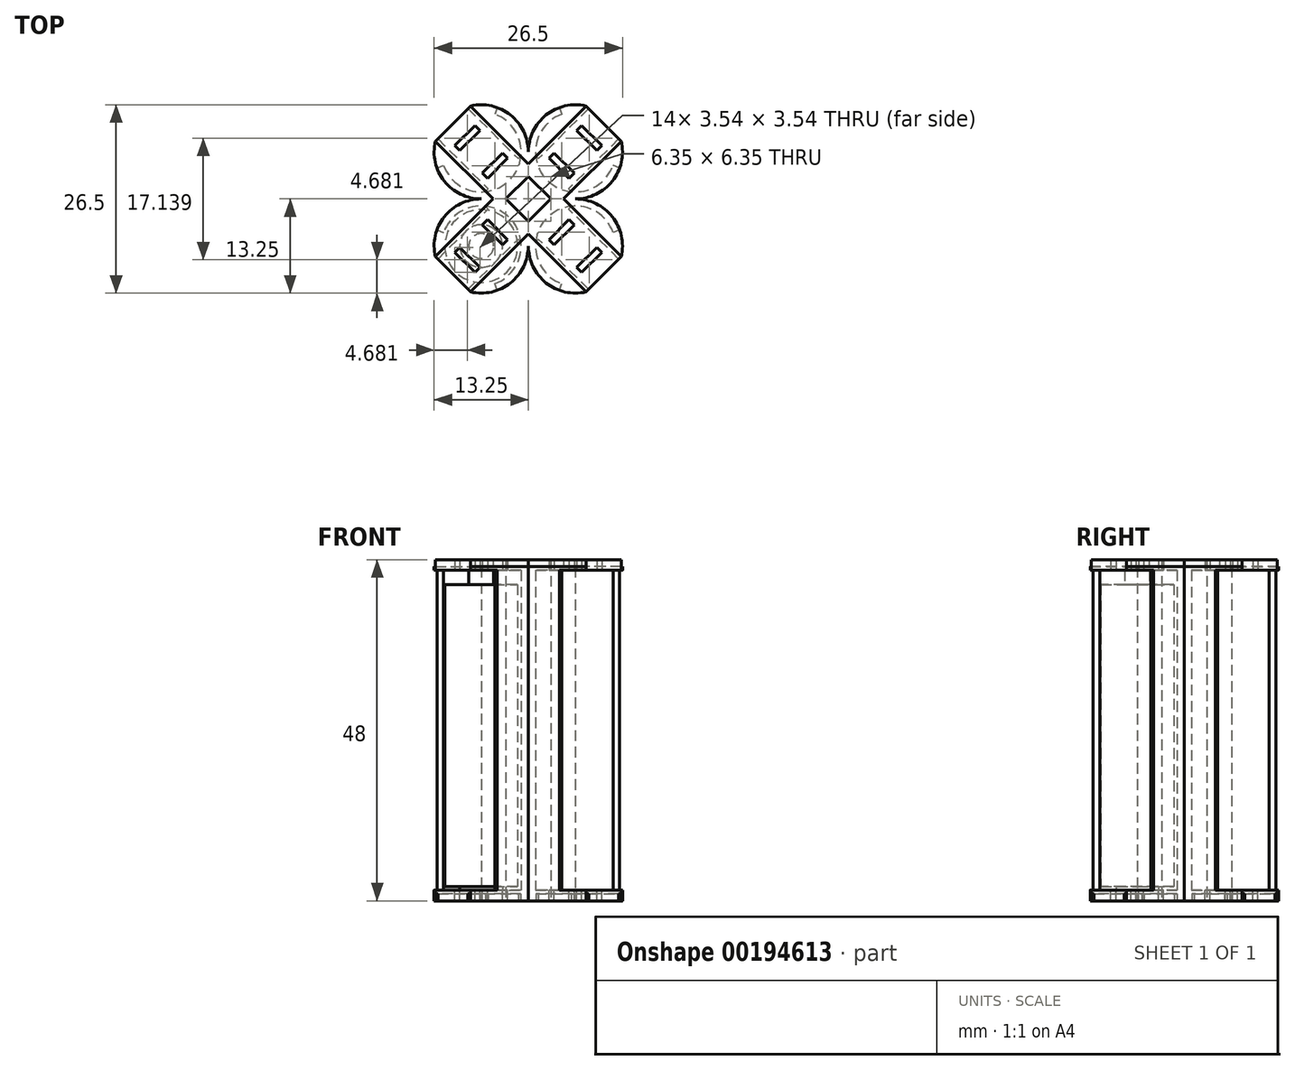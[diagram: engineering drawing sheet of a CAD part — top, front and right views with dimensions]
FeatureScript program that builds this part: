
annotation { "Feature Type Name" : "Feature", "Feature Type Description" : "" }
export const myFeature = defineFeature(function(context is Context, id is Id, definition is map)
    precondition{}
    {
        {
            var Q0;
            Q0=qCreatedBy(makeId("Top.planeOp"),FACE);
            var sketch = newSketch(context, id + "F0", { "sketchPlane" : qUnion([Q0])});
            skCircle(sketch, "E0", {"center": v(-6.62, 6.63) * mm, "radius": 5.62 * mm});
            skLineSegment(sketch, "E1", {"start": v(0, 0) * mm, "end": v(0, 20) * mm, "construction": true});
            skLineSegment(sketch, "E2", {"start": v(0, 0) * mm, "end": v(-20, 0) * mm, "construction": true});
            skCircle(sketch, "E3", {"center": v(-6.62, 6.63) * mm, "radius": 5.12 * mm, "construction": true});
            skArc(sketch, "E4", {"start": v(0, 6.63) * mm, "mid": v(-1.2, 10.42) * mm, "end": v(-4.36, 12.85) * mm});
            skLineSegment(sketch, "E5", {"start": v(-4.36, 12.85) * mm, "end": v(-4.7, 11.91) * mm});
            skLineSegment(sketch, "E6", {"start": v(-6.62, 6.63) * mm, "end": v(-1.5, 6.63) * mm, "construction": true});
            skLineSegment(sketch, "E7", {"start": v(0, 0) * mm, "end": v(-6.63, 6.63) * mm, "construction": true});
            skArc(sketch, "E8.MirrorCS", {"start": v(-6.63, 0) * mm, "mid": v(-10.42, 1.2) * mm, "end": v(-12.85, 4.36) * mm});
            skLineSegment(sketch, "E9.MirrorCS", {"start": v(-12.85, 4.36) * mm, "end": v(-11.91, 4.7) * mm});
            skLineSegment(sketch, "E10", {"start": v(-3.17, 0) * mm, "end": v(0, 3.17) * mm});
            skLineSegment(sketch, "E11.MirrorCS", {"start": v(4.36, 12.85) * mm, "end": v(4.7, 11.91) * mm});
            skArc(sketch, "E12.MirrorCS", {"start": v(0, 6.63) * mm, "mid": v(1.2, 10.42) * mm, "end": v(4.36, 12.85) * mm});
            skCircle(sketch, "E13.MirrorC", {"center": v(6.62, 6.63) * mm, "radius": 5.62 * mm});
            skLineSegment(sketch, "E14.MirrorCS", {"start": v(12.85, 4.36) * mm, "end": v(11.91, 4.7) * mm});
            skArc(sketch, "E15.MirrorCS", {"start": v(6.63, 0) * mm, "mid": v(10.42, 1.2) * mm, "end": v(12.85, 4.36) * mm});
            skLineSegment(sketch, "E16.MirrorCS", {"start": v(3.17, 0) * mm, "end": v(0, 3.17) * mm});
            skArc(sketch, "E17.MirrorCS", {"start": v(-6.63, 0) * mm, "mid": v(-10.42, -1.2) * mm, "end": v(-12.85, -4.36) * mm});
            skLineSegment(sketch, "E18.MirrorCS", {"start": v(-12.85, -4.36) * mm, "end": v(-11.91, -4.7) * mm});
            skCircle(sketch, "E19.MirrorC", {"center": v(-6.62, -6.63) * mm, "radius": 5.62 * mm});
            skLineSegment(sketch, "E20.MirrorCS", {"start": v(-4.36, -12.85) * mm, "end": v(-4.7, -11.91) * mm});
            skArc(sketch, "E21.MirrorCS", {"start": v(0, -6.63) * mm, "mid": v(-1.2, -10.42) * mm, "end": v(-4.36, -12.85) * mm});
            skArc(sketch, "E22.MirrorCS", {"start": v(0, -6.63) * mm, "mid": v(1.2, -10.42) * mm, "end": v(4.36, -12.85) * mm});
            skLineSegment(sketch, "E23.MirrorCS", {"start": v(4.36, -12.85) * mm, "end": v(4.7, -11.91) * mm});
            skLineSegment(sketch, "E24.MirrorCS", {"start": v(12.85, -4.36) * mm, "end": v(11.91, -4.7) * mm});
            skArc(sketch, "E25.MirrorCS", {"start": v(6.63, 0) * mm, "mid": v(10.42, -1.2) * mm, "end": v(12.85, -4.36) * mm});
            skCircle(sketch, "E26.MirrorC", {"center": v(6.62, -6.63) * mm, "radius": 5.62 * mm});
            skLineSegment(sketch, "E27.MirrorCS", {"start": v(3.17, 0) * mm, "end": v(0, -3.17) * mm});
            skLineSegment(sketch, "E28.MirrorCS", {"start": v(-3.17, 0) * mm, "end": v(0, -3.17) * mm});
            skSolve(sketch);
        }
        {
            var Q0;
            Q0=makeQuery(id+"F0.imprint","IMPRINT",FACE,{"disambiguationData":[TD([[makeQuery(id+"F0.imprint","IMPRINT",EDGE,{"derivedFrom":sQuery(id+"F0.wireOp",EDGE,"E4")}),1.0]])]});
            extrude(context, id + "F1", {"entities" : qUnion([Q0]), "endBound" : BoundingType.SYMMETRIC, "depth" : 45 * mm});
        }
        {
            var Q0;
            Q0=makeQuery(id+"F1.opExtrude","CAP_FACE",FACE,{"disambiguationData":[OSD([sQuery(id+"F0.wireOp",EDGE,"E0"),sQuery(id+"F0.wireOp",EDGE,"E4"),sQuery(id+"F0.wireOp",EDGE,"E5"),sQuery(id+"F0.wireOp",EDGE,"E8.MirrorCS"),sQuery(id+"F0.wireOp",EDGE,"E9.MirrorCS"),sQuery(id+"F0.wireOp",EDGE,"E10"),sQuery(id+"F0.wireOp",EDGE,"E11.MirrorCS"),sQuery(id+"F0.wireOp",EDGE,"E12.MirrorCS"),sQuery(id+"F0.wireOp",EDGE,"E13.MirrorC"),sQuery(id+"F0.wireOp",EDGE,"E14.MirrorCS"),sQuery(id+"F0.wireOp",EDGE,"E15.MirrorCS"),sQuery(id+"F0.wireOp",EDGE,"E16.MirrorCS"),sQuery(id+"F0.wireOp",EDGE,"E17.MirrorCS"),sQuery(id+"F0.wireOp",EDGE,"E18.MirrorCS"),sQuery(id+"F0.wireOp",EDGE,"E19.MirrorC"),sQuery(id+"F0.wireOp",EDGE,"E20.MirrorCS"),sQuery(id+"F0.wireOp",EDGE,"E21.MirrorCS"),sQuery(id+"F0.wireOp",EDGE,"E22.MirrorCS"),sQuery(id+"F0.wireOp",EDGE,"E23.MirrorCS"),sQuery(id+"F0.wireOp",EDGE,"E24.MirrorCS"),sQuery(id+"F0.wireOp",EDGE,"E25.MirrorCS"),sQuery(id+"F0.wireOp",EDGE,"E26.MirrorC"),sQuery(id+"F0.wireOp",EDGE,"E27.MirrorCS"),sQuery(id+"F0.wireOp",EDGE,"E28.MirrorCS")])],"isStart":true});
            var sketch = newSketch(context, id + "F2", { "sketchPlane" : qUnion([Q0])});
            skCircle(sketch, "E29", {"center": v(-6.62, 6.63) * mm, "radius": 5.12 * mm});
            skSolve(sketch);
        }
        {
            var Q0;
            Q0 = qSketchRegion(id + "F2", true);
            extrude(context, id + "F3", {"entities" : qUnion([Q0]), "oppositeDirection" : true, "depth" : 43 * mm});
        }
        {
            var Q0;
            Q0=makeQuery(id+"F3.opExtrude","CAP_FACE",FACE,{"disambiguationData":[OSD([sQuery(id+"F2.wireOp",EDGE,"E29")])],"isStart":false});
            var sketch = newSketch(context, id + "F4", { "sketchPlane" : qUnion([Q0])});
            skCircle(sketch, "E30", {"center": v(-6.62, -6.63) * mm, "radius": 1.75 * mm});
            skSolve(sketch);
        }
        {
            var Q0;
            Q0 = qSketchRegion(id + "F4", true);
            extrude(context, id + "F5", {"entities" : qUnion([Q0]), "operationType" : NewBodyOperationType.ADD, "depth" : 2 * mm});
        }
        {
            var Q0;
            Q0=makeQuery(id+"F3.opExtrude","CAP_FACE",FACE,{"disambiguationData":[OSD([sQuery(id+"F2.wireOp",EDGE,"E29")])],"isStart":true});
            var sketch = newSketch(context, id + "F6", { "sketchPlane" : qUnion([Q0])});
            skCircle(sketch, "E31", {"center": v(-6.62, 6.63) * mm, "radius": 5.12 * mm});
            skCircle(sketch, "E32", {"center": v(-6.62, 6.63) * mm, "radius": 3 * mm});
            skSolve(sketch);
        }
        {
            var Q0;
            Q0=makeQuery(id+"F6.imprint","IMPRINT",FACE,{"disambiguationData":[TD([[makeQuery(id+"F6.imprint","IMPRINT",EDGE,{"derivedFrom":sQuery(id+"F6.wireOp",EDGE,"E31")}),1.0]])]});
            extrude(context, id + "F7", {"entities" : qUnion([Q0]), "operationType" : NewBodyOperationType.REMOVE, "oppositeDirection" : true, "depth" : .5 * mm});
        }
        {
            var Q0;
            Q0=makeQuery(id+"F1.opExtrude","CAP_FACE",FACE,{"disambiguationData":[OSD([sQuery(id+"F0.wireOp",EDGE,"E0"),sQuery(id+"F0.wireOp",EDGE,"E4"),sQuery(id+"F0.wireOp",EDGE,"E5"),sQuery(id+"F0.wireOp",EDGE,"E8.MirrorCS"),sQuery(id+"F0.wireOp",EDGE,"E9.MirrorCS"),sQuery(id+"F0.wireOp",EDGE,"E10"),sQuery(id+"F0.wireOp",EDGE,"E11.MirrorCS"),sQuery(id+"F0.wireOp",EDGE,"E12.MirrorCS"),sQuery(id+"F0.wireOp",EDGE,"E13.MirrorC"),sQuery(id+"F0.wireOp",EDGE,"E14.MirrorCS"),sQuery(id+"F0.wireOp",EDGE,"E15.MirrorCS"),sQuery(id+"F0.wireOp",EDGE,"E16.MirrorCS"),sQuery(id+"F0.wireOp",EDGE,"E17.MirrorCS"),sQuery(id+"F0.wireOp",EDGE,"E18.MirrorCS"),sQuery(id+"F0.wireOp",EDGE,"E19.MirrorC"),sQuery(id+"F0.wireOp",EDGE,"E20.MirrorCS"),sQuery(id+"F0.wireOp",EDGE,"E21.MirrorCS"),sQuery(id+"F0.wireOp",EDGE,"E22.MirrorCS"),sQuery(id+"F0.wireOp",EDGE,"E23.MirrorCS"),sQuery(id+"F0.wireOp",EDGE,"E24.MirrorCS"),sQuery(id+"F0.wireOp",EDGE,"E25.MirrorCS"),sQuery(id+"F0.wireOp",EDGE,"E26.MirrorC"),sQuery(id+"F0.wireOp",EDGE,"E27.MirrorCS"),sQuery(id+"F0.wireOp",EDGE,"E28.MirrorCS")])],"isStart":false});
            var sketch = newSketch(context, id + "F8", { "sketchPlane" : qUnion([Q0])});
            skCircle(sketch, "E33", {"center": v(-6.62, -6.63) * mm, "radius": 6.63 * mm});
            skLineSegment(sketch, "E34", {"start": v(0, 0) * mm, "end": v(0, -15) * mm, "construction": true});
            skLineSegment(sketch, "E35", {"start": v(0, 0) * mm, "end": v(-15, 0) * mm, "construction": true});
            skLineSegment(sketch, "E36", {"start": v(-9.63, -6.8) * mm, "end": v(-10.34, -7.5) * mm});
            skLineSegment(sketch, "E37", {"start": v(-10.34, -7.5) * mm, "end": v(-7.5, -10.34) * mm});
            skLineSegment(sketch, "E38", {"start": v(-7.5, -10.34) * mm, "end": v(-6.8, -9.63) * mm});
            skLineSegment(sketch, "E39", {"start": v(-6.8, -9.63) * mm, "end": v(-9.63, -6.8) * mm});
            skLineSegment(sketch, "E40", {"start": v(0, 0) * mm, "end": v(-8.22, -8.22) * mm, "construction": true});
            skLineSegment(sketch, "E41", {"start": v(-6.62, -6.63) * mm, "end": v(-2.65, -10.6) * mm, "construction": true});
            skLineSegment(sketch, "E42.MirrorCS", {"start": v(-3.62, -6.45) * mm, "end": v(-6.45, -3.62) * mm});
            skLineSegment(sketch, "E43.MirrorCS", {"start": v(-2.91, -5.74) * mm, "end": v(-3.62, -6.45) * mm});
            skLineSegment(sketch, "E44.MirrorCS", {"start": v(-6.45, -3.62) * mm, "end": v(-5.74, -2.91) * mm});
            skLineSegment(sketch, "E45.MirrorCS", {"start": v(-5.74, -2.91) * mm, "end": v(-2.91, -5.74) * mm});
            skCircle(sketch, "E46.MirrorC", {"center": v(6.62, -6.63) * mm, "radius": 6.63 * mm});
            skLineSegment(sketch, "E47.MirrorCS", {"start": v(5.74, -2.91) * mm, "end": v(2.91, -5.74) * mm});
            skLineSegment(sketch, "E48.MirrorCS", {"start": v(2.91, -5.74) * mm, "end": v(3.62, -6.45) * mm});
            skLineSegment(sketch, "E49.MirrorCS", {"start": v(3.62, -6.45) * mm, "end": v(6.45, -3.62) * mm});
            skLineSegment(sketch, "E50.MirrorCS", {"start": v(6.45, -3.62) * mm, "end": v(5.74, -2.91) * mm});
            skLineSegment(sketch, "E51.MirrorCS", {"start": v(6.8, -9.63) * mm, "end": v(9.63, -6.8) * mm});
            skLineSegment(sketch, "E52.MirrorCS", {"start": v(7.5, -10.34) * mm, "end": v(6.8, -9.63) * mm});
            skLineSegment(sketch, "E53.MirrorCS", {"start": v(10.34, -7.5) * mm, "end": v(7.5, -10.34) * mm});
            skLineSegment(sketch, "E54.MirrorCS", {"start": v(9.63, -6.8) * mm, "end": v(10.34, -7.5) * mm});
            skCircle(sketch, "E55.MirrorC", {"center": v(-6.62, 6.63) * mm, "radius": 6.63 * mm});
            skCircle(sketch, "E56.MirrorC", {"center": v(6.62, 6.63) * mm, "radius": 6.63 * mm});
            skLineSegment(sketch, "E57.MirrorCS", {"start": v(-5.74, 2.91) * mm, "end": v(-2.91, 5.74) * mm});
            skLineSegment(sketch, "E58.MirrorCS", {"start": v(-3.62, 6.45) * mm, "end": v(-6.45, 3.62) * mm});
            skLineSegment(sketch, "E59.MirrorCS", {"start": v(-6.8, 9.63) * mm, "end": v(-9.63, 6.8) * mm});
            skLineSegment(sketch, "E60.MirrorCS", {"start": v(-10.34, 7.5) * mm, "end": v(-7.5, 10.34) * mm});
            skLineSegment(sketch, "E61.MirrorCS", {"start": v(5.74, 2.91) * mm, "end": v(2.91, 5.74) * mm});
            skLineSegment(sketch, "E62.MirrorCS", {"start": v(3.62, 6.45) * mm, "end": v(6.45, 3.62) * mm});
            skLineSegment(sketch, "E63.MirrorCS", {"start": v(6.8, 9.63) * mm, "end": v(9.63, 6.8) * mm});
            skLineSegment(sketch, "E64.MirrorCS", {"start": v(10.34, 7.5) * mm, "end": v(7.5, 10.34) * mm});
            skLineSegment(sketch, "E65.MirrorCS", {"start": v(9.63, 6.8) * mm, "end": v(10.34, 7.5) * mm});
            skLineSegment(sketch, "E66.MirrorCS", {"start": v(7.5, 10.34) * mm, "end": v(6.8, 9.63) * mm});
            skLineSegment(sketch, "E67.MirrorCS", {"start": v(6.45, 3.62) * mm, "end": v(5.74, 2.91) * mm});
            skLineSegment(sketch, "E68.MirrorCS", {"start": v(2.91, 5.74) * mm, "end": v(3.62, 6.45) * mm});
            skLineSegment(sketch, "E69.MirrorCS", {"start": v(-2.91, 5.74) * mm, "end": v(-3.62, 6.45) * mm});
            skLineSegment(sketch, "E70.MirrorCS", {"start": v(-6.45, 3.62) * mm, "end": v(-5.74, 2.91) * mm});
            skLineSegment(sketch, "E71.MirrorCS", {"start": v(-9.63, 6.8) * mm, "end": v(-10.34, 7.5) * mm});
            skLineSegment(sketch, "E72.MirrorCS", {"start": v(-7.5, 10.34) * mm, "end": v(-6.8, 9.63) * mm});
            skLineSegment(sketch, "E73", {"start": v(-3.17, 0) * mm, "end": v(0, 3.17) * mm});
            skLineSegment(sketch, "E74", {"start": v(0, 3.17) * mm, "end": v(3.17, 0) * mm});
            skLineSegment(sketch, "E75", {"start": v(3.17, 0) * mm, "end": v(0, -3.17) * mm});
            skLineSegment(sketch, "E76", {"start": v(0, -3.17) * mm, "end": v(-3.17, 0) * mm});
            skSolve(sketch);
        }
        {
            var Q0;
            Q0 = qSketchRegion(id + "F8", true);
            extrude(context, id + "F9", {"entities" : qUnion([Q0]), "operationType" : NewBodyOperationType.ADD, "depth" : .5 * mm});
        }
        {
            var Q0;
            Q0=makeQuery(id+"F1.opExtrude","CAP_FACE",FACE,{"disambiguationData":[OSD([sQuery(id+"F0.wireOp",EDGE,"E0"),sQuery(id+"F0.wireOp",EDGE,"E4"),sQuery(id+"F0.wireOp",EDGE,"E5"),sQuery(id+"F0.wireOp",EDGE,"E8.MirrorCS"),sQuery(id+"F0.wireOp",EDGE,"E9.MirrorCS"),sQuery(id+"F0.wireOp",EDGE,"E10"),sQuery(id+"F0.wireOp",EDGE,"E11.MirrorCS"),sQuery(id+"F0.wireOp",EDGE,"E12.MirrorCS"),sQuery(id+"F0.wireOp",EDGE,"E13.MirrorC"),sQuery(id+"F0.wireOp",EDGE,"E14.MirrorCS"),sQuery(id+"F0.wireOp",EDGE,"E15.MirrorCS"),sQuery(id+"F0.wireOp",EDGE,"E16.MirrorCS"),sQuery(id+"F0.wireOp",EDGE,"E17.MirrorCS"),sQuery(id+"F0.wireOp",EDGE,"E18.MirrorCS"),sQuery(id+"F0.wireOp",EDGE,"E19.MirrorC"),sQuery(id+"F0.wireOp",EDGE,"E20.MirrorCS"),sQuery(id+"F0.wireOp",EDGE,"E21.MirrorCS"),sQuery(id+"F0.wireOp",EDGE,"E22.MirrorCS"),sQuery(id+"F0.wireOp",EDGE,"E23.MirrorCS"),sQuery(id+"F0.wireOp",EDGE,"E24.MirrorCS"),sQuery(id+"F0.wireOp",EDGE,"E25.MirrorCS"),sQuery(id+"F0.wireOp",EDGE,"E26.MirrorC"),sQuery(id+"F0.wireOp",EDGE,"E27.MirrorCS"),sQuery(id+"F0.wireOp",EDGE,"E28.MirrorCS")])],"isStart":true});
            var sketch = newSketch(context, id + "F10", { "sketchPlane" : qUnion([Q0])});
            skCircle(sketch, "E77", {"center": v(-6.62, -6.62) * mm, "radius": 6.63 * mm});
            skLineSegment(sketch, "E78", {"start": v(0, 0) * mm, "end": v(0, -15) * mm, "construction": true});
            skLineSegment(sketch, "E79", {"start": v(0, 0) * mm, "end": v(-15, 0) * mm, "construction": true});
            skLineSegment(sketch, "E80", {"start": v(-9.63, -6.8) * mm, "end": v(-10.34, -7.5) * mm});
            skLineSegment(sketch, "E81", {"start": v(-10.34, -7.5) * mm, "end": v(-7.5, -10.34) * mm});
            skLineSegment(sketch, "E82", {"start": v(-7.5, -10.34) * mm, "end": v(-6.8, -9.63) * mm});
            skLineSegment(sketch, "E83", {"start": v(-6.8, -9.63) * mm, "end": v(-9.63, -6.8) * mm});
            skLineSegment(sketch, "E84", {"start": v(0, 0) * mm, "end": v(-8.22, -8.22) * mm, "construction": true});
            skLineSegment(sketch, "E85", {"start": v(-6.62, -6.62) * mm, "end": v(-1.94, -11.3) * mm, "construction": true});
            skLineSegment(sketch, "E86.MirrorCS", {"start": v(-3.62, -6.45) * mm, "end": v(-6.45, -3.62) * mm});
            skLineSegment(sketch, "E87.MirrorCS", {"start": v(-2.91, -5.74) * mm, "end": v(-3.62, -6.45) * mm});
            skLineSegment(sketch, "E88.MirrorCS", {"start": v(-6.45, -3.62) * mm, "end": v(-5.74, -2.91) * mm});
            skLineSegment(sketch, "E89.MirrorCS", {"start": v(-5.74, -2.91) * mm, "end": v(-2.91, -5.74) * mm});
            skCircle(sketch, "E90.MirrorC", {"center": v(6.62, -6.62) * mm, "radius": 6.63 * mm});
            skLineSegment(sketch, "E91.MirrorCS", {"start": v(5.74, -2.91) * mm, "end": v(2.91, -5.74) * mm});
            skLineSegment(sketch, "E92.MirrorCS", {"start": v(2.91, -5.74) * mm, "end": v(3.62, -6.45) * mm});
            skLineSegment(sketch, "E93.MirrorCS", {"start": v(3.62, -6.45) * mm, "end": v(6.45, -3.62) * mm});
            skLineSegment(sketch, "E94.MirrorCS", {"start": v(6.45, -3.62) * mm, "end": v(5.74, -2.91) * mm});
            skLineSegment(sketch, "E95.MirrorCS", {"start": v(6.8, -9.63) * mm, "end": v(9.63, -6.8) * mm});
            skLineSegment(sketch, "E96.MirrorCS", {"start": v(7.5, -10.34) * mm, "end": v(6.8, -9.63) * mm});
            skLineSegment(sketch, "E97.MirrorCS", {"start": v(10.34, -7.5) * mm, "end": v(7.5, -10.34) * mm});
            skLineSegment(sketch, "E98.MirrorCS", {"start": v(9.63, -6.8) * mm, "end": v(10.34, -7.5) * mm});
            skCircle(sketch, "E99.MirrorC", {"center": v(-6.62, 6.63) * mm, "radius": 6.63 * mm});
            skCircle(sketch, "E100.MirrorC", {"center": v(6.62, 6.63) * mm, "radius": 6.63 * mm});
            skLineSegment(sketch, "E101.MirrorCS", {"start": v(-5.74, 2.91) * mm, "end": v(-2.91, 5.74) * mm});
            skLineSegment(sketch, "E102.MirrorCS", {"start": v(-3.62, 6.45) * mm, "end": v(-6.45, 3.62) * mm});
            skLineSegment(sketch, "E103.MirrorCS", {"start": v(-6.8, 9.63) * mm, "end": v(-9.63, 6.8) * mm});
            skLineSegment(sketch, "E104.MirrorCS", {"start": v(-10.34, 7.5) * mm, "end": v(-7.5, 10.34) * mm});
            skLineSegment(sketch, "E105.MirrorCS", {"start": v(5.74, 2.91) * mm, "end": v(2.91, 5.74) * mm});
            skLineSegment(sketch, "E106.MirrorCS", {"start": v(3.62, 6.45) * mm, "end": v(6.45, 3.62) * mm});
            skLineSegment(sketch, "E107.MirrorCS", {"start": v(6.8, 9.63) * mm, "end": v(9.63, 6.8) * mm});
            skLineSegment(sketch, "E108.MirrorCS", {"start": v(10.34, 7.5) * mm, "end": v(7.5, 10.34) * mm});
            skLineSegment(sketch, "E109.MirrorCS", {"start": v(9.63, 6.8) * mm, "end": v(10.34, 7.5) * mm});
            skLineSegment(sketch, "E110.MirrorCS", {"start": v(7.5, 10.34) * mm, "end": v(6.8, 9.63) * mm});
            skLineSegment(sketch, "E111.MirrorCS", {"start": v(6.45, 3.62) * mm, "end": v(5.74, 2.91) * mm});
            skLineSegment(sketch, "E112.MirrorCS", {"start": v(2.91, 5.74) * mm, "end": v(3.62, 6.45) * mm});
            skLineSegment(sketch, "E113.MirrorCS", {"start": v(-2.91, 5.74) * mm, "end": v(-3.62, 6.45) * mm});
            skLineSegment(sketch, "E114.MirrorCS", {"start": v(-6.45, 3.62) * mm, "end": v(-5.74, 2.91) * mm});
            skLineSegment(sketch, "E115.MirrorCS", {"start": v(-9.63, 6.8) * mm, "end": v(-10.34, 7.5) * mm});
            skLineSegment(sketch, "E116.MirrorCS", {"start": v(-7.5, 10.34) * mm, "end": v(-6.8, 9.63) * mm});
            skLineSegment(sketch, "E117", {"start": v(-3.17, 0) * mm, "end": v(0, 3.17) * mm});
            skLineSegment(sketch, "E118", {"start": v(0, 3.17) * mm, "end": v(3.17, 0) * mm});
            skLineSegment(sketch, "E119", {"start": v(3.17, 0) * mm, "end": v(0, -3.17) * mm});
            skLineSegment(sketch, "E120", {"start": v(0, -3.17) * mm, "end": v(-3.17, 0) * mm});
            skSolve(sketch);
        }
        {
            var Q0;
            Q0 = qSketchRegion(id + "F10", true);
            extrude(context, id + "F11", {"entities" : qUnion([Q0]), "operationType" : NewBodyOperationType.ADD, "depth" : 1.5 * mm});
        }
        {
            var Q0;
            Q0=makeQuery(id+"F9.opExtrude","CAP_FACE",FACE,{"disambiguationData":[OSD([sQuery(id+"F8.wireOp",EDGE,"E33"),sQuery(id+"F8.wireOp",EDGE,"E36"),sQuery(id+"F8.wireOp",EDGE,"E37"),sQuery(id+"F8.wireOp",EDGE,"E38"),sQuery(id+"F8.wireOp",EDGE,"E39"),sQuery(id+"F8.wireOp",EDGE,"E42.MirrorCS"),sQuery(id+"F8.wireOp",EDGE,"E43.MirrorCS"),sQuery(id+"F8.wireOp",EDGE,"E44.MirrorCS"),sQuery(id+"F8.wireOp",EDGE,"E45.MirrorCS"),sQuery(id+"F8.wireOp",EDGE,"E46.MirrorC"),sQuery(id+"F8.wireOp",EDGE,"E47.MirrorCS"),sQuery(id+"F8.wireOp",EDGE,"E48.MirrorCS"),sQuery(id+"F8.wireOp",EDGE,"E49.MirrorCS"),sQuery(id+"F8.wireOp",EDGE,"E50.MirrorCS"),sQuery(id+"F8.wireOp",EDGE,"E51.MirrorCS"),sQuery(id+"F8.wireOp",EDGE,"E52.MirrorCS"),sQuery(id+"F8.wireOp",EDGE,"E53.MirrorCS"),sQuery(id+"F8.wireOp",EDGE,"E54.MirrorCS"),sQuery(id+"F8.wireOp",EDGE,"E55.MirrorC"),sQuery(id+"F8.wireOp",EDGE,"E56.MirrorC"),sQuery(id+"F8.wireOp",EDGE,"E57.MirrorCS"),sQuery(id+"F8.wireOp",EDGE,"E58.MirrorCS"),sQuery(id+"F8.wireOp",EDGE,"E59.MirrorCS"),sQuery(id+"F8.wireOp",EDGE,"E60.MirrorCS"),sQuery(id+"F8.wireOp",EDGE,"E61.MirrorCS"),sQuery(id+"F8.wireOp",EDGE,"E62.MirrorCS"),sQuery(id+"F8.wireOp",EDGE,"E63.MirrorCS"),sQuery(id+"F8.wireOp",EDGE,"E64.MirrorCS"),sQuery(id+"F8.wireOp",EDGE,"E65.MirrorCS"),sQuery(id+"F8.wireOp",EDGE,"E66.MirrorCS"),sQuery(id+"F8.wireOp",EDGE,"E67.MirrorCS"),sQuery(id+"F8.wireOp",EDGE,"E68.MirrorCS"),sQuery(id+"F8.wireOp",EDGE,"E69.MirrorCS"),sQuery(id+"F8.wireOp",EDGE,"E70.MirrorCS"),sQuery(id+"F8.wireOp",EDGE,"E71.MirrorCS"),sQuery(id+"F8.wireOp",EDGE,"E72.MirrorCS"),sQuery(id+"F8.wireOp",EDGE,"E73"),sQuery(id+"F8.wireOp",EDGE,"E74"),sQuery(id+"F8.wireOp",EDGE,"E75"),sQuery(id+"F8.wireOp",EDGE,"E76")])],"isStart":false});
            var sketch = newSketch(context, id + "F12", { "sketchPlane" : qUnion([Q0])});
            skLineSegment(sketch, "E121", {"start": v(0, 0) * mm, "end": v(-6.63, 0) * mm, "construction": true});
            skLineSegment(sketch, "E122", {"start": v(0, 0) * mm, "end": v(0, 6.63) * mm, "construction": true});
            skLineSegment(sketch, "E123", {"start": v(-10.34, 7.5) * mm, "end": v(-7.5, 10.34) * mm});
            skLineSegment(sketch, "E124", {"start": v(-7.5, 10.34) * mm, "end": v(-6.8, 9.63) * mm});
            skLineSegment(sketch, "E125", {"start": v(-6.8, 9.63) * mm, "end": v(-9.63, 6.8) * mm});
            skLineSegment(sketch, "E126", {"start": v(-9.63, 6.8) * mm, "end": v(-10.34, 7.5) * mm});
            skLineSegment(sketch, "E127", {"start": v(-6.45, 3.62) * mm, "end": v(-3.62, 6.45) * mm});
            skLineSegment(sketch, "E128", {"start": v(-3.62, 6.45) * mm, "end": v(-2.91, 5.74) * mm});
            skLineSegment(sketch, "E129", {"start": v(-2.91, 5.74) * mm, "end": v(-5.74, 2.91) * mm});
            skLineSegment(sketch, "E130", {"start": v(-5.74, 2.91) * mm, "end": v(-6.45, 3.62) * mm});
            skLineSegment(sketch, "E131", {"start": v(0, 4.95) * mm, "end": v(-8.13, 13.08) * mm});
            skLineSegment(sketch, "E132", {"start": v(-8.13, 13.08) * mm, "end": v(-13.08, 8.13) * mm});
            skLineSegment(sketch, "E133", {"start": v(-13.08, 8.13) * mm, "end": v(-4.95, 0) * mm});
            skLineSegment(sketch, "E134", {"start": v(-3.17, 0) * mm, "end": v(0, 3.17) * mm});
            skLineSegment(sketch, "E135.MirrorCS", {"start": v(3.17, 0) * mm, "end": v(0, 3.17) * mm});
            skLineSegment(sketch, "E136.MirrorCS", {"start": v(0, 4.95) * mm, "end": v(8.13, 13.08) * mm});
            skLineSegment(sketch, "E137.MirrorCS", {"start": v(8.13, 13.08) * mm, "end": v(13.08, 8.13) * mm});
            skLineSegment(sketch, "E138.MirrorCS", {"start": v(13.08, 8.13) * mm, "end": v(4.95, 0) * mm});
            skLineSegment(sketch, "E139.MirrorCS", {"start": v(9.63, 6.8) * mm, "end": v(10.34, 7.5) * mm});
            skLineSegment(sketch, "E140.MirrorCS", {"start": v(6.8, 9.63) * mm, "end": v(9.63, 6.8) * mm});
            skLineSegment(sketch, "E141.MirrorCS", {"start": v(10.34, 7.5) * mm, "end": v(7.5, 10.34) * mm});
            skLineSegment(sketch, "E142.MirrorCS", {"start": v(7.5, 10.34) * mm, "end": v(6.8, 9.63) * mm});
            skLineSegment(sketch, "E143.MirrorCS", {"start": v(3.62, 6.45) * mm, "end": v(2.91, 5.74) * mm});
            skLineSegment(sketch, "E144.MirrorCS", {"start": v(6.45, 3.62) * mm, "end": v(3.62, 6.45) * mm});
            skLineSegment(sketch, "E145.MirrorCS", {"start": v(5.74, 2.91) * mm, "end": v(6.45, 3.62) * mm});
            skLineSegment(sketch, "E146.MirrorCS", {"start": v(2.91, 5.74) * mm, "end": v(5.74, 2.91) * mm});
            skLineSegment(sketch, "E147.MirrorCS", {"start": v(-13.08, -8.13) * mm, "end": v(-4.95, 0) * mm});
            skLineSegment(sketch, "E148.MirrorCS", {"start": v(0, -4.95) * mm, "end": v(-8.13, -13.08) * mm});
            skLineSegment(sketch, "E149.MirrorCS", {"start": v(-8.13, -13.08) * mm, "end": v(-13.08, -8.13) * mm});
            skLineSegment(sketch, "E150.MirrorCS", {"start": v(0, -4.95) * mm, "end": v(8.13, -13.08) * mm});
            skLineSegment(sketch, "E151.MirrorCS", {"start": v(8.13, -13.08) * mm, "end": v(13.08, -8.13) * mm});
            skLineSegment(sketch, "E152.MirrorCS", {"start": v(13.08, -8.13) * mm, "end": v(4.95, 0) * mm});
            skLineSegment(sketch, "E153.MirrorCS", {"start": v(3.17, 0) * mm, "end": v(0, -3.17) * mm});
            skLineSegment(sketch, "E154.MirrorCS", {"start": v(-3.17, 0) * mm, "end": v(0, -3.17) * mm});
            skLineSegment(sketch, "E155.MirrorCS", {"start": v(2.91, -5.74) * mm, "end": v(5.74, -2.91) * mm});
            skLineSegment(sketch, "E156.MirrorCS", {"start": v(6.45, -3.62) * mm, "end": v(3.62, -6.45) * mm});
            skLineSegment(sketch, "E157.MirrorCS", {"start": v(6.8, -9.63) * mm, "end": v(9.63, -6.8) * mm});
            skLineSegment(sketch, "E158.MirrorCS", {"start": v(10.34, -7.5) * mm, "end": v(7.5, -10.34) * mm});
            skLineSegment(sketch, "E159.MirrorCS", {"start": v(9.63, -6.8) * mm, "end": v(10.34, -7.5) * mm});
            skLineSegment(sketch, "E160.MirrorCS", {"start": v(7.5, -10.34) * mm, "end": v(6.8, -9.63) * mm});
            skLineSegment(sketch, "E161.MirrorCS", {"start": v(5.74, -2.91) * mm, "end": v(6.45, -3.62) * mm});
            skLineSegment(sketch, "E162.MirrorCS", {"start": v(3.62, -6.45) * mm, "end": v(2.91, -5.74) * mm});
            skLineSegment(sketch, "E163.MirrorCS", {"start": v(-2.91, -5.74) * mm, "end": v(-5.74, -2.91) * mm});
            skLineSegment(sketch, "E164.MirrorCS", {"start": v(-6.45, -3.62) * mm, "end": v(-3.62, -6.45) * mm});
            skLineSegment(sketch, "E165.MirrorCS", {"start": v(-6.8, -9.63) * mm, "end": v(-9.63, -6.8) * mm});
            skLineSegment(sketch, "E166.MirrorCS", {"start": v(-10.34, -7.5) * mm, "end": v(-7.5, -10.34) * mm});
            skLineSegment(sketch, "E167.MirrorCS", {"start": v(-7.5, -10.34) * mm, "end": v(-6.8, -9.63) * mm});
            skLineSegment(sketch, "E168.MirrorCS", {"start": v(-9.63, -6.8) * mm, "end": v(-10.34, -7.5) * mm});
            skLineSegment(sketch, "E169.MirrorCS", {"start": v(-5.74, -2.91) * mm, "end": v(-6.45, -3.62) * mm});
            skLineSegment(sketch, "E170.MirrorCS", {"start": v(-3.62, -6.45) * mm, "end": v(-2.91, -5.74) * mm});
            skSolve(sketch);
        }
        {
            var Q0;
            Q0=makeQuery(id+"F12.imprint","IMPRINT",FACE,{"disambiguationData":[TD([[makeQuery(id+"F12.imprint","IMPRINT",EDGE,{"derivedFrom":sQuery(id+"F12.wireOp",EDGE,"E123")}),1.0]])]});
            extrude(context, id + "F13", {"entities" : qUnion([Q0]), "operationType" : NewBodyOperationType.ADD, "depth" : 1 * mm});
        }
        {
            var Q0;
            {var subQ0=sQuery(id+"F8.wireOp",EDGE,"E46.MirrorC");var subQ1=makeQuery(id+"F9.opExtrude","CAP_FACE",FACE,{"disambiguationData":[OSD([sQuery(id+"F8.wireOp",EDGE,"E33"),sQuery(id+"F8.wireOp",EDGE,"E36"),sQuery(id+"F8.wireOp",EDGE,"E37"),sQuery(id+"F8.wireOp",EDGE,"E38"),sQuery(id+"F8.wireOp",EDGE,"E39"),sQuery(id+"F8.wireOp",EDGE,"E42.MirrorCS"),sQuery(id+"F8.wireOp",EDGE,"E43.MirrorCS"),sQuery(id+"F8.wireOp",EDGE,"E44.MirrorCS"),sQuery(id+"F8.wireOp",EDGE,"E45.MirrorCS"),subQ0,sQuery(id+"F8.wireOp",EDGE,"E47.MirrorCS"),sQuery(id+"F8.wireOp",EDGE,"E48.MirrorCS"),sQuery(id+"F8.wireOp",EDGE,"E49.MirrorCS"),sQuery(id+"F8.wireOp",EDGE,"E50.MirrorCS"),sQuery(id+"F8.wireOp",EDGE,"E51.MirrorCS"),sQuery(id+"F8.wireOp",EDGE,"E52.MirrorCS"),sQuery(id+"F8.wireOp",EDGE,"E53.MirrorCS"),sQuery(id+"F8.wireOp",EDGE,"E54.MirrorCS"),sQuery(id+"F8.wireOp",EDGE,"E55.MirrorC"),sQuery(id+"F8.wireOp",EDGE,"E56.MirrorC"),sQuery(id+"F8.wireOp",EDGE,"E57.MirrorCS"),sQuery(id+"F8.wireOp",EDGE,"E58.MirrorCS"),sQuery(id+"F8.wireOp",EDGE,"E59.MirrorCS"),sQuery(id+"F8.wireOp",EDGE,"E60.MirrorCS"),sQuery(id+"F8.wireOp",EDGE,"E61.MirrorCS"),sQuery(id+"F8.wireOp",EDGE,"E62.MirrorCS"),sQuery(id+"F8.wireOp",EDGE,"E63.MirrorCS"),sQuery(id+"F8.wireOp",EDGE,"E64.MirrorCS"),sQuery(id+"F8.wireOp",EDGE,"E65.MirrorCS"),sQuery(id+"F8.wireOp",EDGE,"E66.MirrorCS"),sQuery(id+"F8.wireOp",EDGE,"E67.MirrorCS"),sQuery(id+"F8.wireOp",EDGE,"E68.MirrorCS"),sQuery(id+"F8.wireOp",EDGE,"E69.MirrorCS"),sQuery(id+"F8.wireOp",EDGE,"E70.MirrorCS"),sQuery(id+"F8.wireOp",EDGE,"E71.MirrorCS"),sQuery(id+"F8.wireOp",EDGE,"E72.MirrorCS"),sQuery(id+"F8.wireOp",EDGE,"E73"),sQuery(id+"F8.wireOp",EDGE,"E74"),sQuery(id+"F8.wireOp",EDGE,"E75"),sQuery(id+"F8.wireOp",EDGE,"E76")])],"isStart":false});Q0=makeQuery(id+"F13.boolean.opBoolean","SPLIT",FACE,{"disambiguationData":[TD([makeQuery(id+"F1.opExtrude","SWEPT_FACE",FACE,{"disambiguationData":[OSD([sQuery(id+"F0.wireOp",EDGE,"E22.MirrorCS")])]}),makeQuery(id+"F1.opExtrude","SWEPT_FACE",FACE,{"disambiguationData":[OSD([sQuery(id+"F0.wireOp",EDGE,"E25.MirrorCS")])]}),subQ1,makeQuery(id+"F9.opExtrude","SWEPT_FACE",FACE,{"disambiguationData":[OSD([subQ0])]}),makeQuery(id+"F11.opExtrude","SWEPT_FACE",FACE,{"disambiguationData":[OSD([sQuery(id+"F10.wireOp",EDGE,"E100.MirrorC")])]}),makeQuery(id+"F13.opExtrude","SWEPT_FACE",FACE,{"disambiguationData":[OSD([sQuery(id+"F12.wireOp",EDGE,"E150.MirrorCS")])]}),makeQuery(id+"F13.opExtrude","SWEPT_FACE",FACE,{"disambiguationData":[OSD([sQuery(id+"F12.wireOp",EDGE,"E151.MirrorCS")])]}),makeQuery(id+"F13.opExtrude","SWEPT_FACE",FACE,{"disambiguationData":[OSD([sQuery(id+"F12.wireOp",EDGE,"E152.MirrorCS")])]})])],"derivedFrom":subQ1});}
            var Q1;
            {var subQ0=sQuery(id+"F8.wireOp",EDGE,"E33");var subQ1=makeQuery(id+"F9.opExtrude","CAP_FACE",FACE,{"disambiguationData":[OSD([subQ0,sQuery(id+"F8.wireOp",EDGE,"E36"),sQuery(id+"F8.wireOp",EDGE,"E37"),sQuery(id+"F8.wireOp",EDGE,"E38"),sQuery(id+"F8.wireOp",EDGE,"E39"),sQuery(id+"F8.wireOp",EDGE,"E42.MirrorCS"),sQuery(id+"F8.wireOp",EDGE,"E43.MirrorCS"),sQuery(id+"F8.wireOp",EDGE,"E44.MirrorCS"),sQuery(id+"F8.wireOp",EDGE,"E45.MirrorCS"),sQuery(id+"F8.wireOp",EDGE,"E46.MirrorC"),sQuery(id+"F8.wireOp",EDGE,"E47.MirrorCS"),sQuery(id+"F8.wireOp",EDGE,"E48.MirrorCS"),sQuery(id+"F8.wireOp",EDGE,"E49.MirrorCS"),sQuery(id+"F8.wireOp",EDGE,"E50.MirrorCS"),sQuery(id+"F8.wireOp",EDGE,"E51.MirrorCS"),sQuery(id+"F8.wireOp",EDGE,"E52.MirrorCS"),sQuery(id+"F8.wireOp",EDGE,"E53.MirrorCS"),sQuery(id+"F8.wireOp",EDGE,"E54.MirrorCS"),sQuery(id+"F8.wireOp",EDGE,"E55.MirrorC"),sQuery(id+"F8.wireOp",EDGE,"E56.MirrorC"),sQuery(id+"F8.wireOp",EDGE,"E57.MirrorCS"),sQuery(id+"F8.wireOp",EDGE,"E58.MirrorCS"),sQuery(id+"F8.wireOp",EDGE,"E59.MirrorCS"),sQuery(id+"F8.wireOp",EDGE,"E60.MirrorCS"),sQuery(id+"F8.wireOp",EDGE,"E61.MirrorCS"),sQuery(id+"F8.wireOp",EDGE,"E62.MirrorCS"),sQuery(id+"F8.wireOp",EDGE,"E63.MirrorCS"),sQuery(id+"F8.wireOp",EDGE,"E64.MirrorCS"),sQuery(id+"F8.wireOp",EDGE,"E65.MirrorCS"),sQuery(id+"F8.wireOp",EDGE,"E66.MirrorCS"),sQuery(id+"F8.wireOp",EDGE,"E67.MirrorCS"),sQuery(id+"F8.wireOp",EDGE,"E68.MirrorCS"),sQuery(id+"F8.wireOp",EDGE,"E69.MirrorCS"),sQuery(id+"F8.wireOp",EDGE,"E70.MirrorCS"),sQuery(id+"F8.wireOp",EDGE,"E71.MirrorCS"),sQuery(id+"F8.wireOp",EDGE,"E72.MirrorCS"),sQuery(id+"F8.wireOp",EDGE,"E73"),sQuery(id+"F8.wireOp",EDGE,"E74"),sQuery(id+"F8.wireOp",EDGE,"E75"),sQuery(id+"F8.wireOp",EDGE,"E76")])],"isStart":false});Q1=makeQuery(id+"F13.boolean.opBoolean","SPLIT",FACE,{"disambiguationData":[TD([makeQuery(id+"F1.opExtrude","SWEPT_FACE",FACE,{"disambiguationData":[OSD([sQuery(id+"F0.wireOp",EDGE,"E17.MirrorCS")])]}),makeQuery(id+"F1.opExtrude","SWEPT_FACE",FACE,{"disambiguationData":[OSD([sQuery(id+"F0.wireOp",EDGE,"E21.MirrorCS")])]}),makeQuery(id+"F9.opExtrude","SWEPT_FACE",FACE,{"disambiguationData":[OSD([subQ0])]}),subQ1,makeQuery(id+"F11.opExtrude","SWEPT_FACE",FACE,{"disambiguationData":[OSD([sQuery(id+"F10.wireOp",EDGE,"E99.MirrorC")])]}),makeQuery(id+"F13.opExtrude","SWEPT_FACE",FACE,{"disambiguationData":[OSD([sQuery(id+"F12.wireOp",EDGE,"E147.MirrorCS")])]}),makeQuery(id+"F13.opExtrude","SWEPT_FACE",FACE,{"disambiguationData":[OSD([sQuery(id+"F12.wireOp",EDGE,"E148.MirrorCS")])]}),makeQuery(id+"F13.opExtrude","SWEPT_FACE",FACE,{"disambiguationData":[OSD([sQuery(id+"F12.wireOp",EDGE,"E149.MirrorCS")])]})])],"derivedFrom":subQ1});}
            var Q2;
            {var subQ0=sQuery(id+"F8.wireOp",EDGE,"E55.MirrorC");var subQ1=makeQuery(id+"F9.opExtrude","CAP_FACE",FACE,{"disambiguationData":[OSD([sQuery(id+"F8.wireOp",EDGE,"E33"),sQuery(id+"F8.wireOp",EDGE,"E36"),sQuery(id+"F8.wireOp",EDGE,"E37"),sQuery(id+"F8.wireOp",EDGE,"E38"),sQuery(id+"F8.wireOp",EDGE,"E39"),sQuery(id+"F8.wireOp",EDGE,"E42.MirrorCS"),sQuery(id+"F8.wireOp",EDGE,"E43.MirrorCS"),sQuery(id+"F8.wireOp",EDGE,"E44.MirrorCS"),sQuery(id+"F8.wireOp",EDGE,"E45.MirrorCS"),sQuery(id+"F8.wireOp",EDGE,"E46.MirrorC"),sQuery(id+"F8.wireOp",EDGE,"E47.MirrorCS"),sQuery(id+"F8.wireOp",EDGE,"E48.MirrorCS"),sQuery(id+"F8.wireOp",EDGE,"E49.MirrorCS"),sQuery(id+"F8.wireOp",EDGE,"E50.MirrorCS"),sQuery(id+"F8.wireOp",EDGE,"E51.MirrorCS"),sQuery(id+"F8.wireOp",EDGE,"E52.MirrorCS"),sQuery(id+"F8.wireOp",EDGE,"E53.MirrorCS"),sQuery(id+"F8.wireOp",EDGE,"E54.MirrorCS"),subQ0,sQuery(id+"F8.wireOp",EDGE,"E56.MirrorC"),sQuery(id+"F8.wireOp",EDGE,"E57.MirrorCS"),sQuery(id+"F8.wireOp",EDGE,"E58.MirrorCS"),sQuery(id+"F8.wireOp",EDGE,"E59.MirrorCS"),sQuery(id+"F8.wireOp",EDGE,"E60.MirrorCS"),sQuery(id+"F8.wireOp",EDGE,"E61.MirrorCS"),sQuery(id+"F8.wireOp",EDGE,"E62.MirrorCS"),sQuery(id+"F8.wireOp",EDGE,"E63.MirrorCS"),sQuery(id+"F8.wireOp",EDGE,"E64.MirrorCS"),sQuery(id+"F8.wireOp",EDGE,"E65.MirrorCS"),sQuery(id+"F8.wireOp",EDGE,"E66.MirrorCS"),sQuery(id+"F8.wireOp",EDGE,"E67.MirrorCS"),sQuery(id+"F8.wireOp",EDGE,"E68.MirrorCS"),sQuery(id+"F8.wireOp",EDGE,"E69.MirrorCS"),sQuery(id+"F8.wireOp",EDGE,"E70.MirrorCS"),sQuery(id+"F8.wireOp",EDGE,"E71.MirrorCS"),sQuery(id+"F8.wireOp",EDGE,"E72.MirrorCS"),sQuery(id+"F8.wireOp",EDGE,"E73"),sQuery(id+"F8.wireOp",EDGE,"E74"),sQuery(id+"F8.wireOp",EDGE,"E75"),sQuery(id+"F8.wireOp",EDGE,"E76")])],"isStart":false});Q2=makeQuery(id+"F13.boolean.opBoolean","SPLIT",FACE,{"disambiguationData":[TD([makeQuery(id+"F1.opExtrude","SWEPT_FACE",FACE,{"disambiguationData":[OSD([sQuery(id+"F0.wireOp",EDGE,"E4")])]}),makeQuery(id+"F1.opExtrude","SWEPT_FACE",FACE,{"disambiguationData":[OSD([sQuery(id+"F0.wireOp",EDGE,"E8.MirrorCS")])]}),subQ1,makeQuery(id+"F9.opExtrude","SWEPT_FACE",FACE,{"disambiguationData":[OSD([subQ0])]}),makeQuery(id+"F11.opExtrude","SWEPT_FACE",FACE,{"disambiguationData":[OSD([sQuery(id+"F10.wireOp",EDGE,"E77")])]}),makeQuery(id+"F13.opExtrude","SWEPT_FACE",FACE,{"disambiguationData":[OSD([sQuery(id+"F12.wireOp",EDGE,"E131")])]}),makeQuery(id+"F13.opExtrude","SWEPT_FACE",FACE,{"disambiguationData":[OSD([sQuery(id+"F12.wireOp",EDGE,"E132")])]}),makeQuery(id+"F13.opExtrude","SWEPT_FACE",FACE,{"disambiguationData":[OSD([sQuery(id+"F12.wireOp",EDGE,"E133")])]})])],"derivedFrom":subQ1});}
            var Q3;
            {var subQ0=sQuery(id+"F8.wireOp",EDGE,"E56.MirrorC");var subQ1=makeQuery(id+"F9.opExtrude","CAP_FACE",FACE,{"disambiguationData":[OSD([sQuery(id+"F8.wireOp",EDGE,"E33"),sQuery(id+"F8.wireOp",EDGE,"E36"),sQuery(id+"F8.wireOp",EDGE,"E37"),sQuery(id+"F8.wireOp",EDGE,"E38"),sQuery(id+"F8.wireOp",EDGE,"E39"),sQuery(id+"F8.wireOp",EDGE,"E42.MirrorCS"),sQuery(id+"F8.wireOp",EDGE,"E43.MirrorCS"),sQuery(id+"F8.wireOp",EDGE,"E44.MirrorCS"),sQuery(id+"F8.wireOp",EDGE,"E45.MirrorCS"),sQuery(id+"F8.wireOp",EDGE,"E46.MirrorC"),sQuery(id+"F8.wireOp",EDGE,"E47.MirrorCS"),sQuery(id+"F8.wireOp",EDGE,"E48.MirrorCS"),sQuery(id+"F8.wireOp",EDGE,"E49.MirrorCS"),sQuery(id+"F8.wireOp",EDGE,"E50.MirrorCS"),sQuery(id+"F8.wireOp",EDGE,"E51.MirrorCS"),sQuery(id+"F8.wireOp",EDGE,"E52.MirrorCS"),sQuery(id+"F8.wireOp",EDGE,"E53.MirrorCS"),sQuery(id+"F8.wireOp",EDGE,"E54.MirrorCS"),sQuery(id+"F8.wireOp",EDGE,"E55.MirrorC"),subQ0,sQuery(id+"F8.wireOp",EDGE,"E57.MirrorCS"),sQuery(id+"F8.wireOp",EDGE,"E58.MirrorCS"),sQuery(id+"F8.wireOp",EDGE,"E59.MirrorCS"),sQuery(id+"F8.wireOp",EDGE,"E60.MirrorCS"),sQuery(id+"F8.wireOp",EDGE,"E61.MirrorCS"),sQuery(id+"F8.wireOp",EDGE,"E62.MirrorCS"),sQuery(id+"F8.wireOp",EDGE,"E63.MirrorCS"),sQuery(id+"F8.wireOp",EDGE,"E64.MirrorCS"),sQuery(id+"F8.wireOp",EDGE,"E65.MirrorCS"),sQuery(id+"F8.wireOp",EDGE,"E66.MirrorCS"),sQuery(id+"F8.wireOp",EDGE,"E67.MirrorCS"),sQuery(id+"F8.wireOp",EDGE,"E68.MirrorCS"),sQuery(id+"F8.wireOp",EDGE,"E69.MirrorCS"),sQuery(id+"F8.wireOp",EDGE,"E70.MirrorCS"),sQuery(id+"F8.wireOp",EDGE,"E71.MirrorCS"),sQuery(id+"F8.wireOp",EDGE,"E72.MirrorCS"),sQuery(id+"F8.wireOp",EDGE,"E73"),sQuery(id+"F8.wireOp",EDGE,"E74"),sQuery(id+"F8.wireOp",EDGE,"E75"),sQuery(id+"F8.wireOp",EDGE,"E76")])],"isStart":false});Q3=makeQuery(id+"F13.boolean.opBoolean","SPLIT",FACE,{"disambiguationData":[TD([makeQuery(id+"F1.opExtrude","SWEPT_FACE",FACE,{"disambiguationData":[OSD([sQuery(id+"F0.wireOp",EDGE,"E12.MirrorCS")])]}),makeQuery(id+"F1.opExtrude","SWEPT_FACE",FACE,{"disambiguationData":[OSD([sQuery(id+"F0.wireOp",EDGE,"E15.MirrorCS")])]}),subQ1,makeQuery(id+"F9.opExtrude","SWEPT_FACE",FACE,{"disambiguationData":[OSD([subQ0])]}),makeQuery(id+"F11.opExtrude","SWEPT_FACE",FACE,{"disambiguationData":[OSD([sQuery(id+"F10.wireOp",EDGE,"E90.MirrorC")])]}),makeQuery(id+"F13.opExtrude","SWEPT_FACE",FACE,{"disambiguationData":[OSD([sQuery(id+"F12.wireOp",EDGE,"E136.MirrorCS")])]}),makeQuery(id+"F13.opExtrude","SWEPT_FACE",FACE,{"disambiguationData":[OSD([sQuery(id+"F12.wireOp",EDGE,"E137.MirrorCS")])]}),makeQuery(id+"F13.opExtrude","SWEPT_FACE",FACE,{"disambiguationData":[OSD([sQuery(id+"F12.wireOp",EDGE,"E138.MirrorCS")])]})])],"derivedFrom":subQ1});}
            extrude(context, id + "F14", {"entities" : qUnion([Q0, Q1, Q2, Q3]), "operationType" : NewBodyOperationType.REMOVE, "endBound" : BoundingType.THROUGH_ALL, "oppositeDirection" : true, "depth" : 25 * mm});
        }
        {
            var Q0;
            Q0=makeQuery(id+"F11.opExtrude","CAP_FACE",FACE,{"disambiguationData":[OSD([sQuery(id+"F10.wireOp",EDGE,"E77"),sQuery(id+"F10.wireOp",EDGE,"E80"),sQuery(id+"F10.wireOp",EDGE,"E81"),sQuery(id+"F10.wireOp",EDGE,"E82"),sQuery(id+"F10.wireOp",EDGE,"E83"),sQuery(id+"F10.wireOp",EDGE,"E86.MirrorCS"),sQuery(id+"F10.wireOp",EDGE,"E87.MirrorCS"),sQuery(id+"F10.wireOp",EDGE,"E88.MirrorCS"),sQuery(id+"F10.wireOp",EDGE,"E89.MirrorCS"),sQuery(id+"F10.wireOp",EDGE,"E90.MirrorC"),sQuery(id+"F10.wireOp",EDGE,"E91.MirrorCS"),sQuery(id+"F10.wireOp",EDGE,"E92.MirrorCS"),sQuery(id+"F10.wireOp",EDGE,"E93.MirrorCS"),sQuery(id+"F10.wireOp",EDGE,"E94.MirrorCS"),sQuery(id+"F10.wireOp",EDGE,"E95.MirrorCS"),sQuery(id+"F10.wireOp",EDGE,"E96.MirrorCS"),sQuery(id+"F10.wireOp",EDGE,"E97.MirrorCS"),sQuery(id+"F10.wireOp",EDGE,"E98.MirrorCS"),sQuery(id+"F10.wireOp",EDGE,"E99.MirrorC"),sQuery(id+"F10.wireOp",EDGE,"E100.MirrorC"),sQuery(id+"F10.wireOp",EDGE,"E101.MirrorCS"),sQuery(id+"F10.wireOp",EDGE,"E102.MirrorCS"),sQuery(id+"F10.wireOp",EDGE,"E103.MirrorCS"),sQuery(id+"F10.wireOp",EDGE,"E104.MirrorCS"),sQuery(id+"F10.wireOp",EDGE,"E105.MirrorCS"),sQuery(id+"F10.wireOp",EDGE,"E106.MirrorCS"),sQuery(id+"F10.wireOp",EDGE,"E107.MirrorCS"),sQuery(id+"F10.wireOp",EDGE,"E108.MirrorCS"),sQuery(id+"F10.wireOp",EDGE,"E109.MirrorCS"),sQuery(id+"F10.wireOp",EDGE,"E110.MirrorCS"),sQuery(id+"F10.wireOp",EDGE,"E111.MirrorCS"),sQuery(id+"F10.wireOp",EDGE,"E112.MirrorCS"),sQuery(id+"F10.wireOp",EDGE,"E113.MirrorCS"),sQuery(id+"F10.wireOp",EDGE,"E114.MirrorCS"),sQuery(id+"F10.wireOp",EDGE,"E115.MirrorCS"),sQuery(id+"F10.wireOp",EDGE,"E116.MirrorCS"),sQuery(id+"F10.wireOp",EDGE,"E117"),sQuery(id+"F10.wireOp",EDGE,"E118"),sQuery(id+"F10.wireOp",EDGE,"E119"),sQuery(id+"F10.wireOp",EDGE,"E120")])],"isStart":false});
            var sketch = newSketch(context, id + "F15", { "sketchPlane" : qUnion([Q0])});
            skLineSegment(sketch, "E171", {"start": v(-12.72, 8.48) * mm, "end": v(-5.65, 1.41) * mm});
            skLineSegment(sketch, "E172", {"start": v(-5.65, 1.41) * mm, "end": v(-6, 1.06) * mm});
            skLineSegment(sketch, "E173", {"start": v(-6, 1.06) * mm, "end": v(-13.08, 8.13) * mm});
            skLineSegment(sketch, "E174", {"start": v(-13.08, 8.13) * mm, "end": v(-12.72, 8.48) * mm});
            skLineSegment(sketch, "E175", {"start": v(0, 0) * mm, "end": v(-10.6, 10.6) * mm, "construction": true});
            skLineSegment(sketch, "E176", {"start": v(0, 0) * mm, "end": v(0, 6.63) * mm, "construction": true});
            skLineSegment(sketch, "E177", {"start": v(0, 0) * mm, "end": v(-6.63, 0) * mm, "construction": true});
            skLineSegment(sketch, "E178.MirrorCS", {"start": v(-8.48, 12.72) * mm, "end": v(-1.41, 5.65) * mm});
            skLineSegment(sketch, "E179.MirrorCS", {"start": v(-1.41, 5.65) * mm, "end": v(-1.06, 6) * mm});
            skLineSegment(sketch, "E180.MirrorCS", {"start": v(-1.06, 6) * mm, "end": v(-8.13, 13.08) * mm});
            skLineSegment(sketch, "E181.MirrorCS", {"start": v(-8.13, 13.08) * mm, "end": v(-8.48, 12.72) * mm});
            skLineSegment(sketch, "E182.MirrorCS", {"start": v(1.06, 6) * mm, "end": v(8.13, 13.08) * mm});
            skLineSegment(sketch, "E183.MirrorCS", {"start": v(8.48, 12.72) * mm, "end": v(1.41, 5.65) * mm});
            skLineSegment(sketch, "E184.MirrorCS", {"start": v(12.72, 8.48) * mm, "end": v(5.65, 1.41) * mm});
            skLineSegment(sketch, "E185.MirrorCS", {"start": v(6, 1.06) * mm, "end": v(13.08, 8.13) * mm});
            skLineSegment(sketch, "E186.MirrorCS", {"start": v(8.13, 13.08) * mm, "end": v(8.48, 12.72) * mm});
            skLineSegment(sketch, "E187.MirrorCS", {"start": v(13.08, 8.13) * mm, "end": v(12.72, 8.48) * mm});
            skLineSegment(sketch, "E188.MirrorCS", {"start": v(5.65, 1.41) * mm, "end": v(6, 1.06) * mm});
            skLineSegment(sketch, "E189.MirrorCS", {"start": v(1.41, 5.65) * mm, "end": v(1.06, 6) * mm});
            skLineSegment(sketch, "E190.MirrorCS", {"start": v(-6, -1.06) * mm, "end": v(-13.08, -8.13) * mm});
            skLineSegment(sketch, "E191.MirrorCS", {"start": v(-12.72, -8.48) * mm, "end": v(-5.65, -1.41) * mm});
            skLineSegment(sketch, "E192.MirrorCS", {"start": v(-8.48, -12.72) * mm, "end": v(-1.41, -5.65) * mm});
            skLineSegment(sketch, "E193.MirrorCS", {"start": v(-1.06, -6) * mm, "end": v(-8.13, -13.08) * mm});
            skLineSegment(sketch, "E194.MirrorCS", {"start": v(1.06, -6) * mm, "end": v(8.13, -13.08) * mm});
            skLineSegment(sketch, "E195.MirrorCS", {"start": v(8.48, -12.72) * mm, "end": v(1.41, -5.65) * mm});
            skLineSegment(sketch, "E196.MirrorCS", {"start": v(12.72, -8.48) * mm, "end": v(5.65, -1.41) * mm});
            skLineSegment(sketch, "E197.MirrorCS", {"start": v(6, -1.06) * mm, "end": v(13.08, -8.13) * mm});
            skLineSegment(sketch, "E198.MirrorCS", {"start": v(5.65, -1.41) * mm, "end": v(6, -1.06) * mm});
            skLineSegment(sketch, "E199.MirrorCS", {"start": v(13.08, -8.13) * mm, "end": v(12.72, -8.48) * mm});
            skLineSegment(sketch, "E200.MirrorCS", {"start": v(8.13, -13.08) * mm, "end": v(8.48, -12.72) * mm});
            skLineSegment(sketch, "E201.MirrorCS", {"start": v(1.41, -5.65) * mm, "end": v(1.06, -6) * mm});
            skLineSegment(sketch, "E202.MirrorCS", {"start": v(-1.41, -5.65) * mm, "end": v(-1.06, -6) * mm});
            skLineSegment(sketch, "E203.MirrorCS", {"start": v(-8.13, -13.08) * mm, "end": v(-8.48, -12.72) * mm});
            skLineSegment(sketch, "E204.MirrorCS", {"start": v(-13.08, -8.13) * mm, "end": v(-12.72, -8.48) * mm});
            skLineSegment(sketch, "E205.MirrorCS", {"start": v(-5.65, -1.41) * mm, "end": v(-6, -1.06) * mm});
            skSolve(sketch);
        }
        {
            var Q0;
            Q0 = qSketchRegion(id + "F15", true);
            extrude(context, id + "F16", {"entities" : qUnion([Q0]), "operationType" : NewBodyOperationType.REMOVE, "oppositeDirection" : true, "depth" : 1 * mm});
        }
    });
